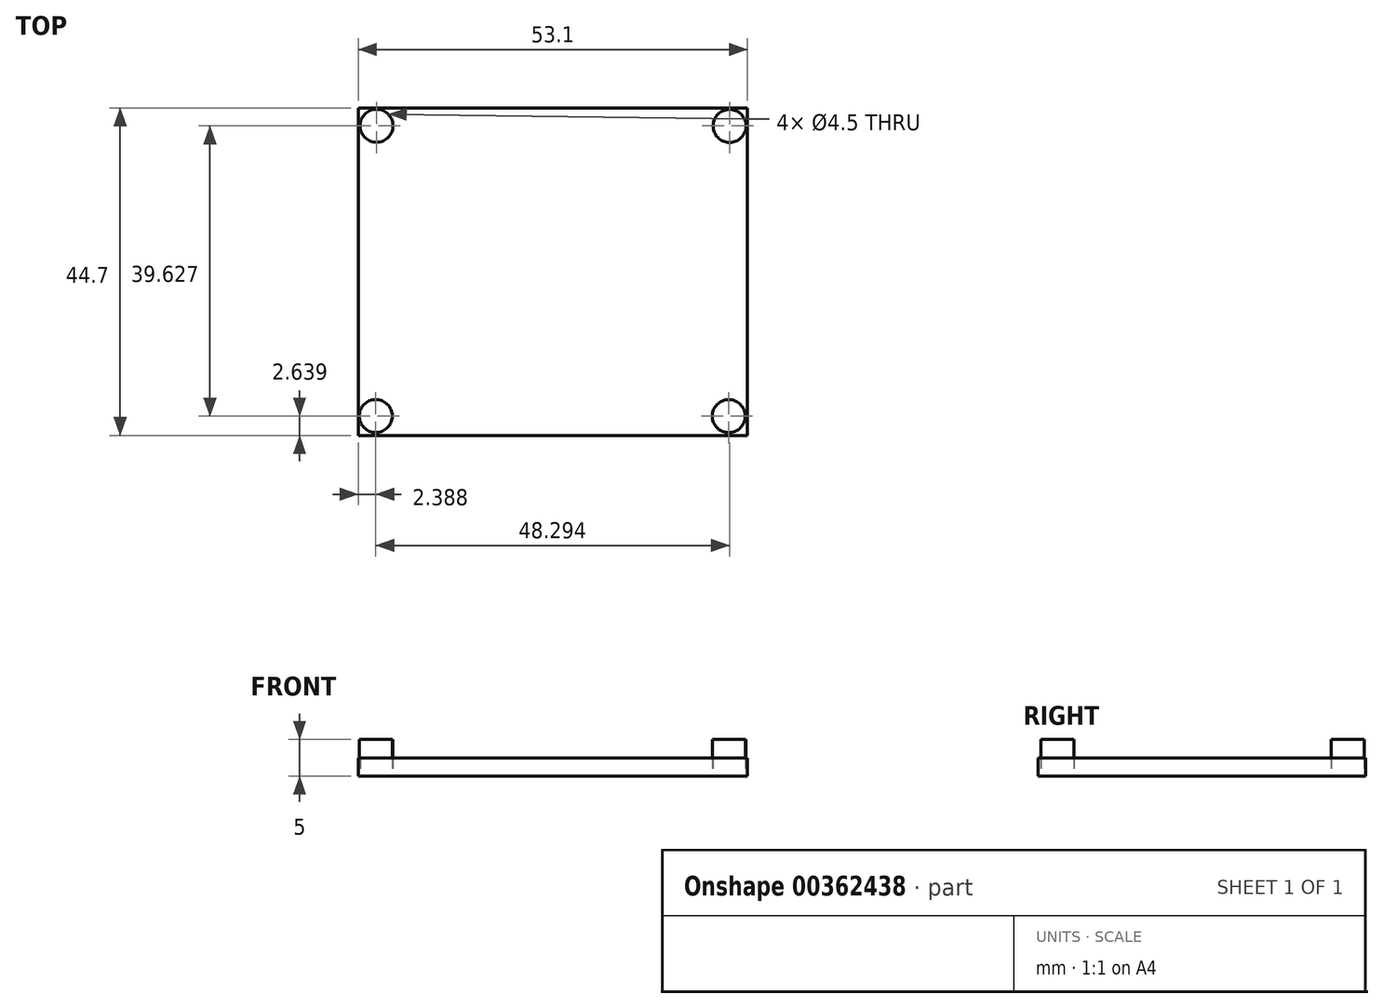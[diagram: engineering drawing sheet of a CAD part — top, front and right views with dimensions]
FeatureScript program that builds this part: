
annotation { "Feature Type Name" : "Feature", "Feature Type Description" : "" }
export const myFeature = defineFeature(function(context is Context, id is Id, definition is map)
    precondition{}
    {
        {
            var Q0;
            Q0=qCreatedBy(makeId("Top.planeOp"),FACE);
            var sketch = newSketch(context, id + "F0", { "sketchPlane" : qUnion([Q0])});
            skLineSegment(sketch, "E0.bottom", {"start": v(26.55, -22.35) * mm, "end": v(-26.55, -22.35) * mm});
            skLineSegment(sketch, "E0.top", {"start": v(26.55, 22.35) * mm, "end": v(-26.55, 22.35) * mm});
            skLineSegment(sketch, "E0.left", {"start": v(26.55, -22.35) * mm, "end": v(26.55, 22.35) * mm});
            skLineSegment(sketch, "E0.right", {"start": v(-26.55, -22.35) * mm, "end": v(-26.55, 22.35) * mm});
            skPoint(sketch, "E0.middle", {"position": v(0, 0) * mm});
            skCircle(sketch, "E1", {"center": v(-24.05, 19.92) * mm, "radius": 2.25 * mm});
            skCircle(sketch, "E2", {"center": v(24.13, 19.9) * mm, "radius": 2.25 * mm});
            skCircle(sketch, "E3", {"center": v(-24.16, -19.7) * mm, "radius": 2.25 * mm});
            skCircle(sketch, "E4", {"center": v(24.02, -19.71) * mm, "radius": 2.25 * mm});
            skSolve(sketch);
        }
        {
            var Q0;
            Q0=makeQuery(id+"F0.imprint","IMPRINT",FACE,{"disambiguationData":[TD([[makeQuery(id+"F0.imprint","IMPRINT",EDGE,{"derivedFrom":sQuery(id+"F0.wireOp",EDGE,"E2")}),1.0]])]});
            var Q1;
            Q1=makeQuery(id+"F0.imprint","IMPRINT",FACE,{"disambiguationData":[TD([[makeQuery(id+"F0.imprint","IMPRINT",EDGE,{"derivedFrom":sQuery(id+"F0.wireOp",EDGE,"E1")}),1.0]])]});
            var Q2;
            Q2=makeQuery(id+"F0.imprint","IMPRINT",FACE,{"disambiguationData":[TD([[makeQuery(id+"F0.imprint","IMPRINT",EDGE,{"derivedFrom":sQuery(id+"F0.wireOp",EDGE,"E3")}),1.0]])]});
            var Q3;
            Q3=makeQuery(id+"F0.imprint","IMPRINT",FACE,{"disambiguationData":[TD([[makeQuery(id+"F0.imprint","IMPRINT",EDGE,{"derivedFrom":sQuery(id+"F0.wireOp",EDGE,"E4")}),1.0]])]});
            extrude(context, id + "F1", {"entities" : qUnion([Q0, Q1, Q2, Q3]), "depth" : 5 * mm});
        }
        {
            var Q0;
            Q0=makeQuery(id+"F0.imprint","IMPRINT",FACE,{"disambiguationData":[TD([[makeQuery(id+"F0.imprint","IMPRINT",EDGE,{"derivedFrom":sQuery(id+"F0.wireOp",EDGE,"E0.bottom")}),-1.0]])]});
            extrude(context, id + "F2", {"entities" : qUnion([Q0]), "depth" : 2.5 * mm});
        }
        {
            var Q0;
            Q0=makeQuery(id+"F1.opExtrude","CAP_FACE",FACE,{"disambiguationData":[OSD([sQuery(id+"F0.wireOp",EDGE,"E1")])],"isStart":false});
            var sketch = newSketch(context, id + "F3", { "sketchPlane" : qUnion([Q0])});
            skSolve(sketch);
        }
        {
            var Q0;
            Q0=makeQuery(id+"F3.imprint","IMPRINT",FACE,{"disambiguationData":[TD([[makeQuery(id+"F3.imprint","IMPRINT",EDGE,{"derivedFrom":makeQuery(id+"F1.opExtrude","CAP_EDGE",EDGE,{"disambiguationData":[OSD([sQuery(id+"F0.wireOp",EDGE,"E1")])],"isStart":false})}),1.0]])]});
            var sketch = newSketch(context, id + "F4", { "sketchPlane" : qUnion([Q0])});
            skCircle(sketch, "E5", {"center": v(-24.05, 19.95) * mm, "radius": 1.25 * mm});
            skCircle(sketch, "E6", {"center": v(-24.18, -19.73) * mm, "radius": 1.25 * mm});
            skCircle(sketch, "E7", {"center": v(24.02, -19.72) * mm, "radius": 1.25 * mm});
            skCircle(sketch, "E8", {"center": v(24.14, 19.9) * mm, "radius": 1.25 * mm});
            skSolve(sketch);
        }
        {
            var Q0;
            Q0=sQuery(id+"F4.wireOp",EDGE,"E6");
            var Q1;
            Q1=sQuery(id+"F4.wireOp",EDGE,"E5");
            var Q2;
            Q2=sQuery(id+"F4.wireOp",EDGE,"E8");
            var Q3;
            Q3=sQuery(id+"F4.wireOp",EDGE,"E7");
            extrude(context, id + "F5", {"bodyType" : ToolBodyType.SURFACE, "surfaceEntities" : qUnion([Q0, Q1, Q2, Q3]), "depth" : 3 * mm});
        }
    });
